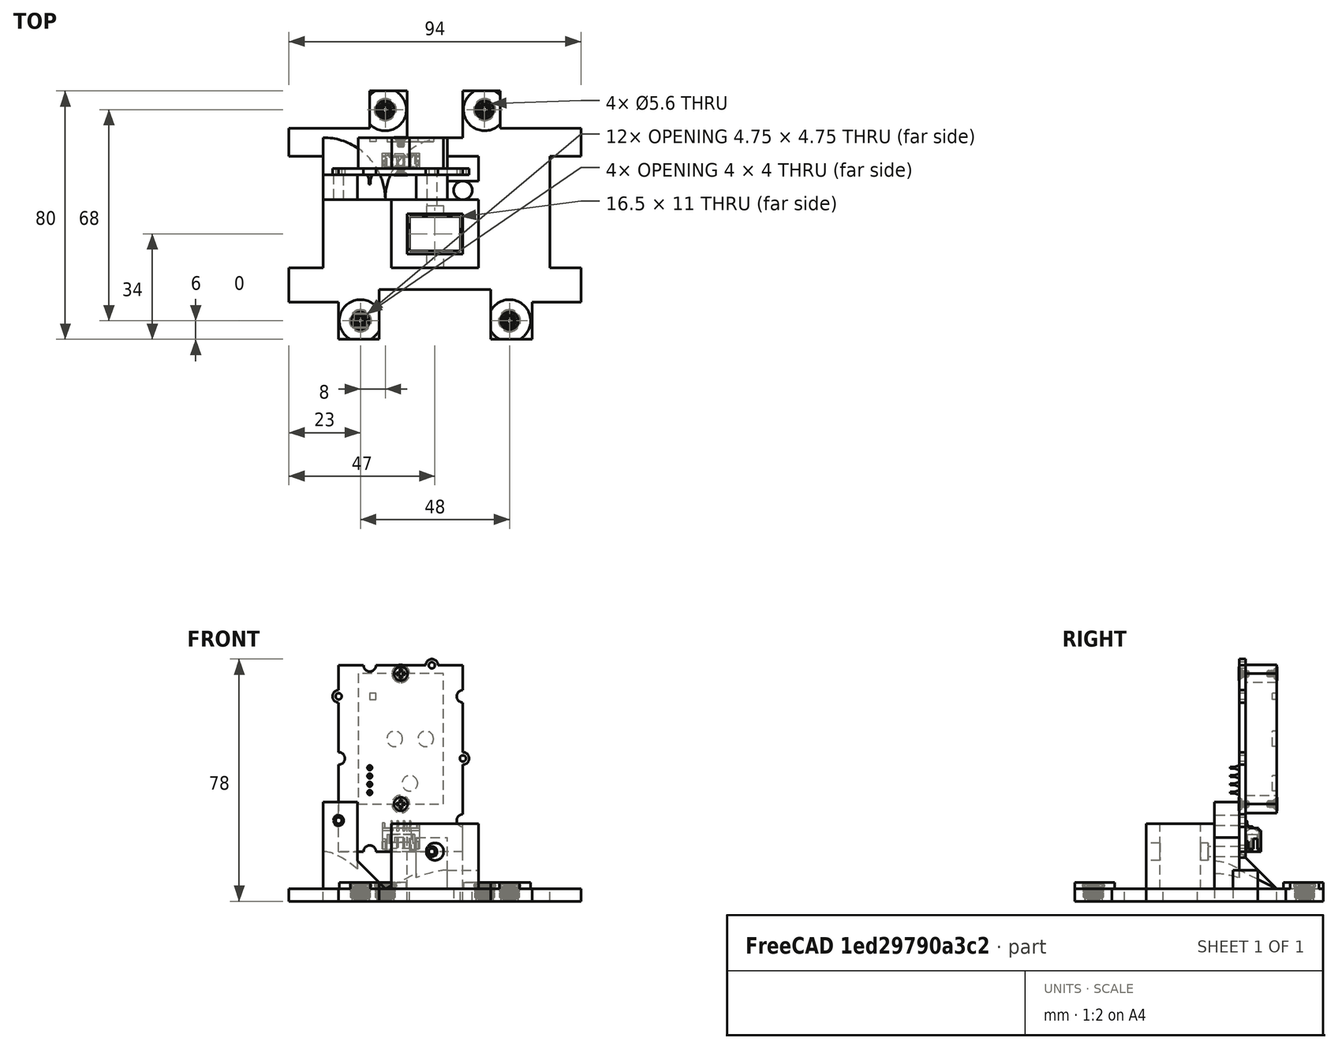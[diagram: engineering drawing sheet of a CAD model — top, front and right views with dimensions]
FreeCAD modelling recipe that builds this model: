
FCSTD DOCUMENT  (FreeCAD 0.20R29410 (Git))
Label: spine_11_03_2022
License: All rights reserved
LicenseURL: http://en.wikipedia.org/wiki/All_rights_reserved
objects: Part::Box×25, Part::Cylinder×18, Part::MultiFuse×16, Part::Cut×5, Part::Feature×5, Part::Cone×2
note: 71 computed .brp shape members not serialized (recipe doc carries the construction recipe); baked Part::Feature solids carry a one-line shape summary decoded from their .brp

FEATURE [Part::Cylinder] Cylinder103  label="Cylinder107"
  Angle = 360
  AttacherType = Attacher::AttachEngine3D
  FirstAngle = 0
  Height = 10
  Placement = pos=(63,3,0) rot=(0,0,1;0rad)
  Radius = 2.25
  SecondAngle = 0
FEATURE [Part::Box] Box064  label="base005"
  AttacherType = Attacher::AttachEngine3D
  Height = 4
  Length = 26
  Placement = pos=(-10.25,68,0) rot=(0,0,1;0rad)
  Width = 12
FEATURE [Part::Box] Box060  label="base001"
  AttacherType = Attacher::AttachEngine3D
  Height = 4
  Length = 94
  Width = 80
FEATURE [Part::Box] Box061  label="base002"
  AttacherType = Attacher::AttachEngine3D
  Height = 4
  Length = 26
  Width = 12
FEATURE [Part::Box] Box062  label="base003"
  AttacherType = Attacher::AttachEngine3D
  Height = 4
  Length = 26
  Placement = pos=(68,0,0) rot=(0,0,1;0rad)
  Width = 12
FEATURE [Part::Cylinder] Cylinder104  label="Cylinder103"
  Angle = 360
  AttacherType = Attacher::AttachEngine3D
  FirstAngle = 0
  Height = 10
  Placement = pos=(71,71,0) rot=(0,0,1;0rad)
  Radius = 2.25
  SecondAngle = 0
FEATURE [Part::Cylinder] Cylinder106  label="Cylinder104"
  Angle = 360
  AttacherType = Attacher::AttachEngine3D
  FirstAngle = 0
  Height = 10
  Placement = pos=(23,71,0) rot=(0,0,1;0rad)
  Radius = 2
  SecondAngle = 0
FEATURE [Part::Cylinder] Cylinder105  label="Cylinder108"
  Angle = 360
  AttacherType = Attacher::AttachEngine3D
  FirstAngle = 0
  Height = 10
  Placement = pos=(31,3,0) rot=(0,0,1;0rad)
  Radius = 2.25
  SecondAngle = 0
FEATURE [Part::Box] Box081  label="Cube039"
  AttacherType = Attacher::AttachEngine3D
  Height = 10
  Length = 10
  Placement = pos=(101.4,27,140) rot=(0,0,1;0rad)
  Width = 36
FEATURE [Part::Box] Box082  label="Cube040"
  AttacherType = Attacher::AttachEngine3D
  Height = 10
  Length = 36
  Placement = pos=(42,1,140) rot=(0,0,1;0rad)
  Width = 19
FEATURE [Part::Box] Box073  label="baseSpineCut"
  AttacherType = Attacher::AttachEngine3D
  Height = 25
  Length = 16.5
  Placement = pos=(51.75,32.5,140) rot=(0,0,1;0rad)
  Width = 11
FEATURE [Part::Cylinder] Cylinder107  label="Cylinder109"
  Angle = 360
  AttacherType = Attacher::AttachEngine3D
  FirstAngle = 0
  Height = 10
  Radius = 1
  SecondAngle = 0
FEATURE [Part::MultiFuse] Fusion123  label="screwIns001"
  Placement = pos=(0,3,0) rot=(0,0,1;0rad)
  Shapes = -> [Cylinder105,Cylinder107,Cylinder103,Cylinder104,Cylinder106]
FEATURE [Part::Box] Box080  label="Cube038"
  AttacherType = Attacher::AttachEngine3D
  Height = 10
  Length = 22
  Placement = pos=(2,27,140) rot=(0,0,1;0rad)
  Width = 22
FEATURE [Part::Box] Box063  label="base004"
  AttacherType = Attacher::AttachEngine3D
  Height = 4
  Length = 26
  Placement = pos=(78,68,0) rot=(0,0,1;0rad)
  Width = 12
FEATURE [Part::MultiFuse] Fusion122
  Shapes = -> [Box064,Box063,Box061,Box062]
FEATURE [Part::Cut] Cut019  label="baseNew"
  Base = -> Box060
  Tool = -> Fusion122
FEATURE [Part::Cut] Cut020  label="baseNew001"
  Base = -> Cut019
  Placement = pos=(107,84,140) rot=(0,0,1;3.14159rad)
  Tool = -> Fusion123
FEATURE [Part::Box] Box083  label="Cube041"
  AttacherType = Attacher::AttachEngine3D
  Height = 25
  Length = 18
  Placement = pos=(51,31.5,144) rot=(0,0,1;0rad)
  Width = 13
FEATURE [Part::Box] Box084  label="Cube042"
  AttacherType = Attacher::AttachEngine3D
  Height = 51
  Length = 50
  Placement = pos=(24,49,140) rot=(0,0,1;0rad)
  Width = 8
FEATURE [Part::Box] Box085  label="Cube043"
  AttacherType = Attacher::AttachEngine3D
  Height = 10
  Length = 15
  Placement = pos=(69,69,140) rot=(0,0,1;1.5708rad)
  Width = 18
FEATURE [Part::Box] Box086  label="baseSpineIn"
  AttacherType = Attacher::AttachEngine3D
  Height = 25
  Length = 28
  Placement = pos=(46,27,140) rot=(0,0,1;0rad)
  Width = 22
FEATURE [Part::Cylinder] Cylinder
  Angle = 360
  AttacherType = Attacher::AttachEngine3D
  FirstAngle = 0
  Height = 50
  Placement = pos=(60,-3,156) rot=(-1,0,0;1.5708rad)
  Radius = 2.8
  SecondAngle = 0
FEATURE [Part::Feature] Feature  label="Seed Grove SCD30"
  Placement = pos=(29,59,156) rot=(0.707107,0,0.707107;3.14159rad)
  shape: bbox 44 x 15.1 x 64 mm, 422 faces, 13 solids (baked)
FEATURE [Part::Cylinder] Cylinder108  label="Cylinder110"
  Angle = 360
  AttacherType = Attacher::AttachEngine3D
  FirstAngle = 0
  Height = 50
  Placement = pos=(80,17,186) rot=(-1,0,0;1.5708rad)
  Radius = 1.65
  SecondAngle = 0
FEATURE [Part::Cylinder] Cylinder109  label="Cylinder111"
  Angle = 360
  AttacherType = Attacher::AttachEngine3D
  FirstAngle = 0
  Height = 50
  Placement = pos=(40,17,166) rot=(-1,0,0;1.5708rad)
  Radius = 1.65
  SecondAngle = 0
FEATURE [Part::Cylinder] Cylinder110  label="Cylinder112"
  Angle = 360
  AttacherType = Attacher::AttachEngine3D
  FirstAngle = 0
  Height = 50
  Placement = pos=(70,17,156) rot=(-1,0,0;1.5708rad)
  Radius = 1.65
  SecondAngle = 0
FEATURE [Part::MultiFuse] Fusion  label="m2Cuts"
  Placement = pos=(-11,30,0) rot=(0,0,1;0rad)
  Shapes = -> [Cylinder108,Cylinder109,Cylinder110]
FEATURE [Part::Box] Box087  label="Cube044"
  AttacherType = Attacher::AttachEngine3D
  Height = 51
  Length = 50
  Placement = pos=(13,49,172) rot=(0,0,1;0rad)
  Width = 8
FEATURE [Part::Box] Box088  label="Cube045"
  AttacherType = Attacher::AttachEngine3D
  Height = 51
  Length = 19
  Placement = pos=(35,49,144) rot=(0,0,1;0rad)
  Width = 8
FEATURE [Part::MultiFuse] Fusion124  label="base"
  Shapes = -> [Cut020,Box084,Box086]
FEATURE [Part::MultiFuse] Fusion125  label="cuts"
  Shapes = -> [Box087,Box088,Fusion,Box085,Box080,Box083,Box082,Box081,Box073,Cylinder]
FEATURE [Part::Box] Box089  label="Cube046"
  AttacherType = Attacher::AttachEngine3D
  Height = 10
  Length = 11
  Placement = pos=(13,57,140) rot=(0,0,1;0rad)
  Width = 6
FEATURE [Part::Feature] Solid  label="m4HeatSet"
  Placement = pos=(36,10,140) rot=(1,0,0;1.5708rad)
  shape: bbox 7.1 x 7.1 x 6.065 mm, 234 faces (baked)
FEATURE [Part::Feature] Solid001  label="m4HeatSet001"
  Placement = pos=(84,10,140) rot=(1,0,0;1.5708rad)
  shape: bbox 7.1 x 7.1 x 6.065 mm, 234 faces (baked)
FEATURE [Part::Feature] Solid002  label="m4HeatSet002"
  Placement = pos=(44,78,140) rot=(1,0,0;1.5708rad)
  shape: bbox 7.1 x 7.1 x 6.065 mm, 234 faces (baked)
FEATURE [Part::Feature] Solid003  label="m4HeatSet003"
  Placement = pos=(76,78,140) rot=(1,0,0;1.5708rad)
  shape: bbox 7.1 x 7.1 x 6.065 mm, 234 faces (baked)
FEATURE [Part::Cylinder] Cylinder111  label="m4HeatSetCut"
  Angle = 360
  AttacherType = Attacher::AttachEngine3D
  FirstAngle = 0
  Height = 10
  Placement = pos=(36,10,140) rot=(0,0,1;0rad)
  Radius = 2.8
  SecondAngle = 0
FEATURE [Part::Cylinder] Cylinder112  label="m4HeatSetCut001"
  Angle = 360
  AttacherType = Attacher::AttachEngine3D
  FirstAngle = 0
  Height = 10
  Placement = pos=(84,10,140) rot=(0,0,1;0rad)
  Radius = 2.8
  SecondAngle = 0
FEATURE [Part::Cylinder] Cylinder113  label="m4HeatSetCut002"
  Angle = 360
  AttacherType = Attacher::AttachEngine3D
  FirstAngle = 0
  Height = 10
  Placement = pos=(76,78,140) rot=(0,0,1;0rad)
  Radius = 2.8
  SecondAngle = 0
FEATURE [Part::Cylinder] Cylinder114  label="m4HeatSetCut003"
  Angle = 360
  AttacherType = Attacher::AttachEngine3D
  FirstAngle = 0
  Height = 10
  Placement = pos=(44,78,140) rot=(0,0,1;0rad)
  Radius = 2.8
  SecondAngle = 0
FEATURE [Part::MultiFuse] Fusion126  label="heatSetCuts"
  Shapes = -> [Cylinder111,Cylinder112,Cylinder113,Cylinder114]
FEATURE [Part::Box] Box091  label="Cube048"
  AttacherType = Attacher::AttachEngine3D
  Height = 10
  Length = 11
  Placement = pos=(13,49,140) rot=(0,0,1;0rad)
  Width = 8
FEATURE [Part::MultiFuse] Fusion127  label="cuts001"
  Shapes = -> [Box091,Fusion126,Box089,Fusion125]
FEATURE [Part::Cylinder] Cylinder115  label="m4HeatSetCut004"
  Angle = 360
  AttacherType = Attacher::AttachEngine3D
  FirstAngle = 0
  Height = 6
  Placement = pos=(36,10,140) rot=(0,0,-1;1.0472rad)
  Radius = 6.8
  SecondAngle = 0
FEATURE [Part::Cylinder] Cylinder116  label="m4HeatSetCut005"
  Angle = 360
  AttacherType = Attacher::AttachEngine3D
  FirstAngle = 0
  Height = 6
  Placement = pos=(84,10,140) rot=(0,0,1;0rad)
  Radius = 6.8
  SecondAngle = 0
FEATURE [Part::Cylinder] Cylinder117  label="m4HeatSetCut006"
  Angle = 360
  AttacherType = Attacher::AttachEngine3D
  FirstAngle = 0
  Height = 6
  Placement = pos=(76,78,140) rot=(0,0,1;0rad)
  Radius = 6.8
  SecondAngle = 0
FEATURE [Part::Cylinder] Cylinder118  label="m4HeatSetCut007"
  Angle = 360
  AttacherType = Attacher::AttachEngine3D
  FirstAngle = 0
  Height = 6
  Placement = pos=(44,78,140) rot=(0,0,1;0rad)
  Radius = 6.8
  SecondAngle = 0
FEATURE [Part::MultiFuse] Fusion128  label="heatSetAddOns"
  Shapes = -> [Cylinder115,Cylinder116,Cylinder117,Cylinder118]
FEATURE [Part::Box] Box092  label="Cube049"
  AttacherType = Attacher::AttachEngine3D
  Height = 10
  Length = 94
  Placement = pos=(13,-4,140) rot=(0,0,1;0rad)
  Width = 8
FEATURE [Part::MultiFuse] Fusion129  label="base006"
  Shapes = -> [Fusion128,Fusion124]
FEATURE [Part::Box] Box093  label="Cube050"
  AttacherType = Attacher::AttachEngine3D
  Height = 10
  Length = 94
  Placement = pos=(13,84,140) rot=(0,0,1;0rad)
  Width = 8
FEATURE [Part::Box] Box094  label="Cube051"
  AttacherType = Attacher::AttachEngine3D
  Height = 10
  Length = 94
  Placement = pos=(89,72,140) rot=(0,0,1;1.5708rad)
  Width = 8
FEATURE [Part::Box] Box095  label="Cube052"
  AttacherType = Attacher::AttachEngine3D
  Height = 10
  Length = 94
  Placement = pos=(39,72,140) rot=(0,0,1;1.5708rad)
  Width = 8
FEATURE [Part::MultiFuse] Fusion130
  Shapes = -> [Box093,Box094,Box095,Box092]
FEATURE [Part::MultiFuse] Fusion131  label="cuts002"
  Shapes = -> [Fusion127,Fusion130]
FEATURE [Part::Box] Box096  label="Cube053"
  AttacherType = Attacher::AttachEngine3D
  Height = 10
  Length = 10
  Placement = pos=(97,27,140) rot=(0,0,1;0rad)
  Width = 36
FEATURE [Part::MultiFuse] Fusion132  label="cuts003"
  Shapes = -> [Fusion131,Box096]
FEATURE [Part::Cut] Cut  label="base007"
  Base = -> Fusion129
  Tool = -> Fusion132
FEATURE [Part::Cone] Cone
  Angle = 90
  AttacherType = Attacher::AttachEngine3D
  Height = 12
  Placement = pos=(24,49,144) rot=(0,0,1;0rad)
  Radius1 = 20
  Radius2 = 8
FEATURE [Part::Box] Box  label="Cube"
  AttacherType = Attacher::AttachEngine3D
  Height = 60
  Length = 11
  Placement = pos=(64,49,144) rot=(0,0,1;0rad)
  Width = 8
FEATURE [Part::Box] Box097  label="Cube054"
  AttacherType = Attacher::AttachEngine3D
  Height = 55
  Length = 11
  Placement = pos=(54,49,160.5) rot=(0,0,1;0rad)
  Width = 8
FEATURE [Part::MultiFuse] Fusion133  label="cuts004"
  Shapes = -> [Box,Box097]
FEATURE [Part::Cut] Cut021
  Base = -> Cut
  Tool = -> Fusion133
FEATURE [Part::Cylinder] Cylinder119  label="m4HeatSetCut008"
  Angle = 360
  AttacherType = Attacher::AttachEngine3D
  FirstAngle = 0
  Height = 10
  Placement = pos=(69,52,140) rot=(0,0,1;0rad)
  Radius = 3
  SecondAngle = 0
FEATURE [Part::MultiFuse] Fusion134
  Shapes = -> [Cone,Cut021]
FEATURE [Part::Cut] Cut022
  Base = -> Fusion134
  Tool = -> Cylinder119
FEATURE [Part::Box] Box098  label="Cube055"
  AttacherType = Attacher::AttachEngine3D
  Height = 10
  Length = 10
  Placement = pos=(64,55,140) rot=(0,0,1;0rad)
  Width = 8
FEATURE [Part::MultiFuse] Fusion135
  Shapes = -> [Cut022,Box098]
FEATURE [Part::Cone] Cone001
  Angle = 90
  AttacherType = Attacher::AttachEngine3D
  Height = 6
  Placement = pos=(64,49,144) rot=(0,0,1;1.5708rad)
  Radius1 = 20
  Radius2 = 8
FEATURE [Part::MultiFuse] Fusion136
  Shapes = -> [Fusion135,Cone001]
